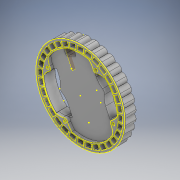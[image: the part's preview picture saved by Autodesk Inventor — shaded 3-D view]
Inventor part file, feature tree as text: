
AUTODESK INVENTOR PART (.ipt)
format: ipt  version: 2020 (Build 240168000, 168)  size: 1,081,344 bytes
history: native  units: mm
features: sketch x10, extrude x7, projected_geometry x3, other x2, hole x2, mirror x1, fillet x1, imported_body x1
ambient origin geometry x8: Origin, YZ Plane, XZ Plane, XY Plane, X Axis, Y Axis, Z Axis, Center Point
bodies: Body1 (feature_tree)
feature tree (27):
  other  "Твердое тело1"
  extrude  "Выдавливание1"  TaperAngle=0.0deg  [1 undecoded]
  sketch  "Эскиз2"
  extrude  "Выдавливание3"  Depth=40.0mm TaperAngle=360.0deg
  sketch  "Эскиз4"
  extrude  "Выдавливание4"  Depth=53.0mm
  extrude  "Выдавливание5"  Depth=82.0mm
  sketch  "Эскиз5"
  hole  "Отверстие1"  [1 undecoded]
  hole  "Отверстие2"  [1 undecoded]
  extrude  "Выдавливание6"  Depth=6.7mm
  other  "РабПлоскость1"
  mirror  "Зеркальное отражение1"
  extrude  "Выдавливание7"  TaperAngle=0.0deg  [1 undecoded]
  fillet  "Сопряжение1"  Radius=20.0mm
  extrude  "Выдавливание8"  Depth=11.0mm TaperAngle=0.0deg
  sketch  "Эскиз10"
  sketch  "Эскиз11"
  sketch  "Эскиз1"
  sketch  "Эскиз3"
  sketch  "Эскиз6"
  sketch  "Эскиз7"
  sketch  "Эскиз8"
  projected_geometry  "Спроецированная петля1"
  projected_geometry  "Спроецированная петля2"
  projected_geometry  "Спроецированная петля3"
  imported_body  "БазТело1"
note: 4 required parameter values undecoded (feature->parameter linkage not recoverable at this tier; creation-order binding heuristic only, values carry confidence <= 0.55)
